# Revit family: Seating-Teknion-NBF__Banqs_Full_Alcove_Solo_Focus-2019
name_source: partatom
category: Furniture Systems
units: mm (PartAtom-declared; Revit-internal decimal feet)

## family parameters
Always vertical = Yes
Cut with Voids When Loaded = No
OmniClass Number = 23.40.70.14.64.21
OmniClass Title = Systems Furniture
Part Type = Normal
Room Calculation Point = No
Round Connector Dimension = Use Diameter
Shared = Yes
Work Plane-Based = No

## types (6) — shared parameters
Assembly Code = E2020200
Electrical Finishes = Plastic - Teknion - 8C - Very White
Manufacturer = Teknion
Manufacturer Fax = 416.661.4586
Part Number = NBF_
Product Line = Banqs
Product Page URL = https://www.teknion.com
Seat Paint Finish = Paint - Teknion - Foundation - Granite
Series = Banqs
Sustainability Data = https://www.teknion.com
URL = www.teknion.com
Unit Weight URL = http://www.teknion.com
Warranty = http://www.teknion.com

## per-type parameters (varying)
| type | Bracket | Description | High and Medium Bracket | Left Sofa Width | Model | Product Documentation Link | Right Sofa Width | Screen Height | Width |
| High Screen Standard Sofa | No | Banqs Full Alcove Solo Focus, High Screen, Standard Sofa | Yes | 25.125 " | NBFHS___ | Banqshttps://www.teknion.com | 25.125 " | 54.975 " | 50.125 " |
| High Screen Wide Sofa | No | Banqs full Alcove Solo Focus, High Screen and Wide Sofa | Yes | 35.12 " | NBFHW___ | https://www.teknion.com | 35.12 " | 54.975 " | 74.125 " |
| Low Screen Standard Sofa | Yes | Banqs Full Alcove Solo Focus, Low Screen, Standard Sofa | No | 25.125 " | NBFLS___ | https://www.teknion.com | 25.125 " | 31.64 " | 50.125 " |
| Low Screen Wide Sofa | Yes | Banqs full Alcove Solo Focus, Low Screen and Wide Sofa | No | 35.12 " | NBFLW___ | https://www.teknion.com | 35.12 " | 31.64 " | 74.125 " |
| Medium Screen Standard Sofa | No | Banqs Full Alcove Solo Focus, Medium Screen, Standard Sofa | Yes | 25.125 " | NBFMS___ | https://www.teknion.com | 25.125 " | 43.974 " | 50.125 " |
| Medium Screen Wide Sofa | No | Banqs full Alcove Solo Focus, Medium Screen and Wide Sofa | Yes | 35.12 " | NBFMW___ | https://www.teknion.com | 35.12 " | 43.974 " | 74.125 " |

## geometry (parser evidence)
native form markers: Sweep x2
no freeform markers — native parametric forms only
